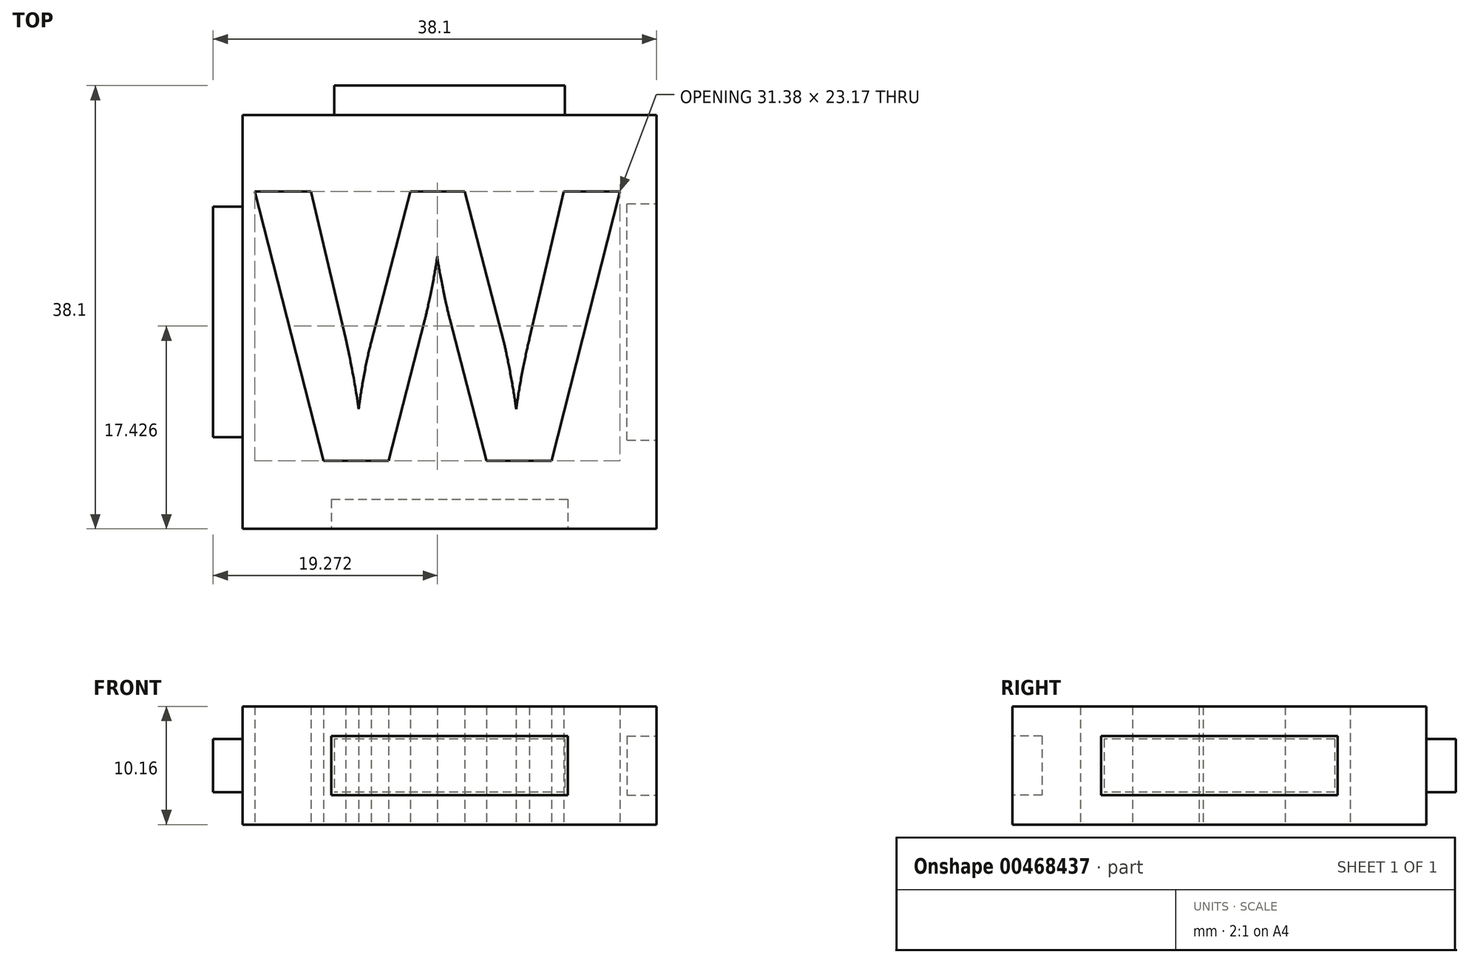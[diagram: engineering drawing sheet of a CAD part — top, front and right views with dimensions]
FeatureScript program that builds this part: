
annotation { "Feature Type Name" : "Feature", "Feature Type Description" : "" }
export const myFeature = defineFeature(function(context is Context, id is Id, definition is map)
    precondition{}
    {
        {
            var Q0;
            Q0=qCreatedBy(makeId("Top.planeOp"),FACE);
            var sketch = newSketch(context, id + "F0", { "sketchPlane" : qUnion([Q0])});
            skLineSegment(sketch, "E0.bottom", {"start": v(-17.78, 17.78) * mm, "end": v(17.78, 17.78) * mm});
            skLineSegment(sketch, "E0.top", {"start": v(-17.78, -17.78) * mm, "end": v(17.78, -17.78) * mm});
            skLineSegment(sketch, "E0.left", {"start": v(-17.78, 17.78) * mm, "end": v(-17.78, -17.78) * mm});
            skLineSegment(sketch, "E0.right", {"start": v(17.78, 17.78) * mm, "end": v(17.78, -17.78) * mm});
            skText(sketch, "E1", { "text": "W", "fontName": "OpenSans-Bold.ttf"});
            const initialGuessF0  = {"E1": [-0.01674, -0.01194, 1, 0, 0.02337]};
            skSetInitialGuess(sketch, initialGuessF0);
            skSolve(sketch);
        }
        {
            var Q0;
            Q0=qSketchRegion(id+"F0",true);
            extrude(context, id + "F1", {"entities" : qUnion([Q0]), "endBound" : BoundingType.SYMMETRIC, "depth" : 10.16 * mm});
        }
        {
            var Q0;
            Q0=makeQuery(id+"F1.opExtrude","SWEPT_FACE",FACE,{"disambiguationData":[OSD([sQuery(id+"F0.wireOp",EDGE,"E0.bottom")])]});
            var sketch = newSketch(context, id + "F2", { "sketchPlane" : qUnion([Q0])});
            skLineSegment(sketch, "E2.bottom", {"start": v(-9.9, 2.29) * mm, "end": v(9.9, 2.29) * mm});
            skLineSegment(sketch, "E2.top", {"start": v(-9.9, -2.29) * mm, "end": v(9.9, -2.29) * mm});
            skLineSegment(sketch, "E2.left", {"start": v(-9.9, 2.29) * mm, "end": v(-9.9, -2.29) * mm});
            skLineSegment(sketch, "E2.right", {"start": v(9.9, 2.29) * mm, "end": v(9.9, -2.29) * mm});
            skSolve(sketch);
        }
        {
            var Q0;
            Q0=qSketchRegion(id+"F2",true);
            extrude(context, id + "F3", {"entities" : qUnion([Q0]), "operationType" : NewBodyOperationType.ADD, "depth" : 2.54 * mm});
        }
        {
            var Q0;
            Q0=makeQuery(id+"F1.opExtrude","SWEPT_FACE",FACE,{"disambiguationData":[OSD([sQuery(id+"F0.wireOp",EDGE,"E0.left")])]});
            var sketch = newSketch(context, id + "F4", { "sketchPlane" : qUnion([Q0])});
            skLineSegment(sketch, "E3.bottom", {"start": v(-9.9, 2.29) * mm, "end": v(9.9, 2.29) * mm});
            skLineSegment(sketch, "E3.top", {"start": v(-9.9, -2.29) * mm, "end": v(9.9, -2.29) * mm});
            skLineSegment(sketch, "E3.left", {"start": v(-9.9, 2.29) * mm, "end": v(-9.9, -2.29) * mm});
            skLineSegment(sketch, "E3.right", {"start": v(9.9, 2.29) * mm, "end": v(9.9, -2.29) * mm});
            skSolve(sketch);
        }
        {
            var Q0;
            Q0=qSketchRegion(id+"F4",true);
            extrude(context, id + "F5", {"entities" : qUnion([Q0]), "operationType" : NewBodyOperationType.ADD, "depth" : 2.54 * mm});
        }
        {
            var Q0;
            Q0=makeQuery(id+"F1.opExtrude","SWEPT_FACE",FACE,{"disambiguationData":[OSD([sQuery(id+"F0.wireOp",EDGE,"E0.top")])]});
            var sketch = newSketch(context, id + "F6", { "sketchPlane" : qUnion([Q0])});
            skLineSegment(sketch, "E4.bottom", {"start": v(-10.16, 2.54) * mm, "end": v(10.16, 2.54) * mm});
            skLineSegment(sketch, "E4.top", {"start": v(-10.16, -2.54) * mm, "end": v(10.16, -2.54) * mm});
            skLineSegment(sketch, "E4.left", {"start": v(-10.16, 2.54) * mm, "end": v(-10.16, -2.54) * mm});
            skLineSegment(sketch, "E4.right", {"start": v(10.16, 2.54) * mm, "end": v(10.16, -2.54) * mm});
            skSolve(sketch);
        }
        {
            var Q0;
            Q0=qSketchRegion(id+"F6",true);
            extrude(context, id + "F7", {"entities" : qUnion([Q0]), "operationType" : NewBodyOperationType.REMOVE, "oppositeDirection" : true, "depth" : 2.54 * mm});
        }
        {
            var Q0;
            Q0=makeQuery(id+"F1.opExtrude","SWEPT_FACE",FACE,{"disambiguationData":[OSD([sQuery(id+"F0.wireOp",EDGE,"E0.right")])]});
            var sketch = newSketch(context, id + "F8", { "sketchPlane" : qUnion([Q0])});
            skLineSegment(sketch, "E5.bottom", {"start": v(-10.16, 2.54) * mm, "end": v(10.16, 2.54) * mm});
            skLineSegment(sketch, "E5.top", {"start": v(-10.16, -2.54) * mm, "end": v(10.16, -2.54) * mm});
            skLineSegment(sketch, "E5.left", {"start": v(-10.16, 2.54) * mm, "end": v(-10.16, -2.54) * mm});
            skLineSegment(sketch, "E5.right", {"start": v(10.16, 2.54) * mm, "end": v(10.16, -2.54) * mm});
            skSolve(sketch);
        }
        {
            var Q0;
            Q0=qSketchRegion(id+"F8",true);
            extrude(context, id + "F9", {"entities" : qUnion([Q0]), "operationType" : NewBodyOperationType.REMOVE, "oppositeDirection" : true, "depth" : 2.54 * mm});
        }
    });
